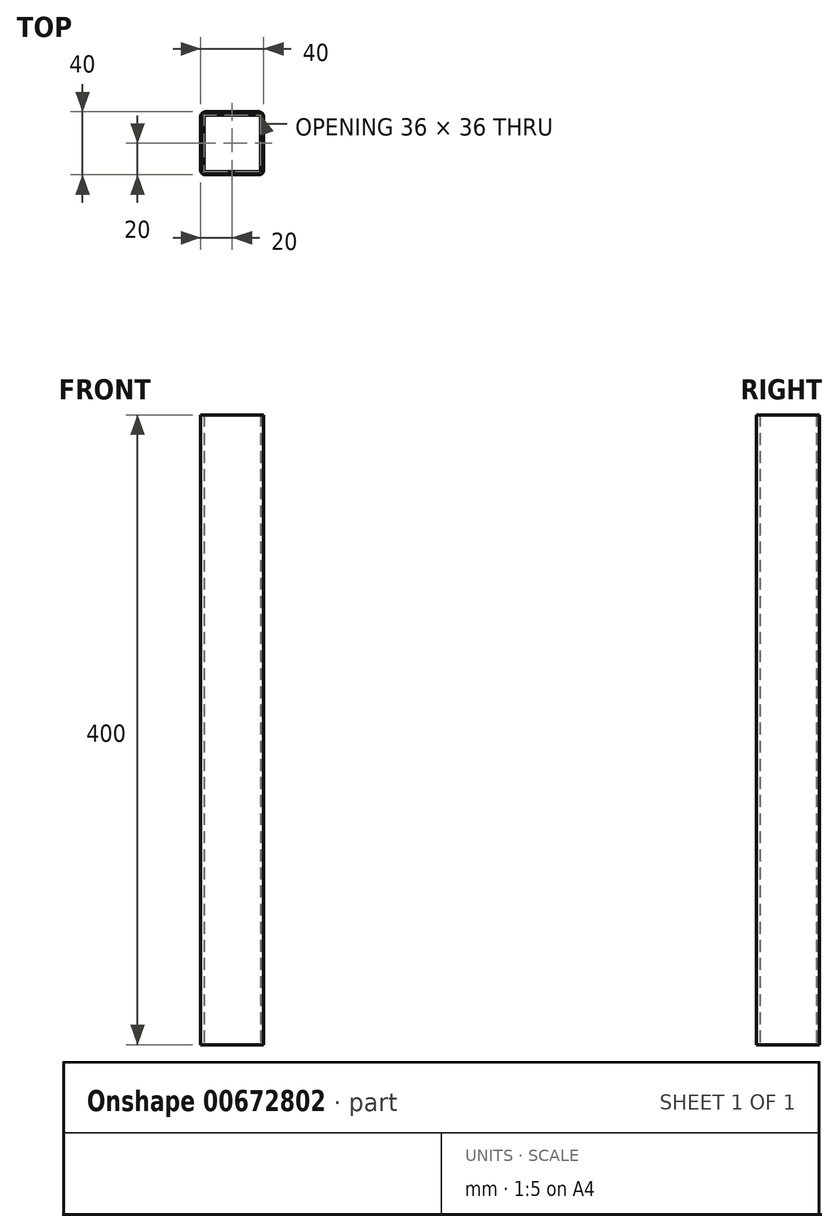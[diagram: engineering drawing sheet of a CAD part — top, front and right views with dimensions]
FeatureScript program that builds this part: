
annotation { "Feature Type Name" : "Feature", "Feature Type Description" : "" }
export const myFeature = defineFeature(function(context is Context, id is Id, definition is map)
    precondition{}
    {
        {
            var Q0;
            Q0=qCreatedBy(makeId("Top.planeOp"),FACE);
            var sketch = newSketch(context, id + "F0", { "sketchPlane" : qUnion([Q0])});
            skLineSegment(sketch, "E0.bottom", {"start": v(-17, 20) * mm, "end": v(17, 20) * mm});
            skLineSegment(sketch, "E0.top", {"start": v(-17, -20) * mm, "end": v(17, -20) * mm});
            skLineSegment(sketch, "E0.left", {"start": v(-20, 17) * mm, "end": v(-20, -17) * mm});
            skLineSegment(sketch, "E0.right", {"start": v(20, 17) * mm, "end": v(20, -17) * mm});
            skPoint(sketch, "E0.middle", {"position": v(0, 0) * mm});
            skPoint(sketch, "E1.visualSharp", {"position": v(-20, 20) * mm});
            skArc(sketch, "E1.filletArc", {"start": v(-17, 20) * mm, "mid": v(-19.12, 19.12) * mm, "end": v(-20, 17) * mm});
            skPoint(sketch, "E2.visualSharp", {"position": v(20, 20) * mm});
            skArc(sketch, "E2.filletArc", {"start": v(20, 17) * mm, "mid": v(19.12, 19.12) * mm, "end": v(17, 20) * mm});
            skPoint(sketch, "E3.visualSharp", {"position": v(20, -20) * mm});
            skArc(sketch, "E3.filletArc", {"start": v(17, -20) * mm, "mid": v(19.12, -19.12) * mm, "end": v(20, -17) * mm});
            skPoint(sketch, "E4.visualSharp", {"position": v(-20, -20) * mm});
            skArc(sketch, "E4.filletArc", {"start": v(-20, -17) * mm, "mid": v(-19.12, -19.12) * mm, "end": v(-17, -20) * mm});
            skArc(sketch, "E5.0", {"start": v(-17, 18) * mm, "mid": v(-17.7, 17.7) * mm, "end": v(-18, 17) * mm});
            skLineSegment(sketch, "E5.1", {"start": v(-18, 17) * mm, "end": v(-18, -17) * mm});
            skLineSegment(sketch, "E5.2", {"start": v(-17, 18) * mm, "end": v(17, 18) * mm});
            skArc(sketch, "E5.3", {"start": v(-18, -17) * mm, "mid": v(-17.7, -17.7) * mm, "end": v(-17, -18) * mm});
            skArc(sketch, "E5.4", {"start": v(18, 17) * mm, "mid": v(17.7, 17.7) * mm, "end": v(17, 18) * mm});
            skLineSegment(sketch, "E5.5", {"start": v(18, 17) * mm, "end": v(18, -17) * mm});
            skArc(sketch, "E5.6", {"start": v(17, -18) * mm, "mid": v(17.7, -17.7) * mm, "end": v(18, -17) * mm});
            skLineSegment(sketch, "E5.7", {"start": v(-17, -18) * mm, "end": v(17, -18) * mm});
            skSolve(sketch);
        }
        {
            var Q0;
            Q0 = qSketchRegion(id + "F0", true);
            extrude(context, id + "F1", {"entities" : qUnion([Q0]), "depth" : 400 * mm, "offsetDistance" : 25 * mm});
        }
    });
